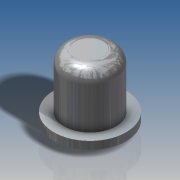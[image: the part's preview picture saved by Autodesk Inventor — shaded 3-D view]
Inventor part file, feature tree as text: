
AUTODESK INVENTOR PART (.ipt)
format: ipt  version: 2016 SP2 (Build 200236200, 236)  size: 137,728 bytes
history: native  units: in
note: dims shown in document units (in); Inventor stores cm internally (conversion verified against a paired STEP export)
features: revolve x1, sketch x1
ambient origin geometry x8: Origin, YZ Plane, XZ Plane, XY Plane, X Axis, Y Axis, Z Axis, Center Point
bodies: Solid1 (feature_tree)
feature tree (2):
  revolve  "Revolution1"  [1 undecoded]
  sketch  "Sketch2"  dims[d0=0.0787in d1=0.0283in d2=0.2205in d3=0.0236in d4=0.1575in d5=0.1654in d6=0.0394in d7=90.0deg]
note: 1 required parameter value undecoded (feature->parameter linkage not recoverable at this tier; creation-order binding heuristic only, values carry confidence <= 0.55)
